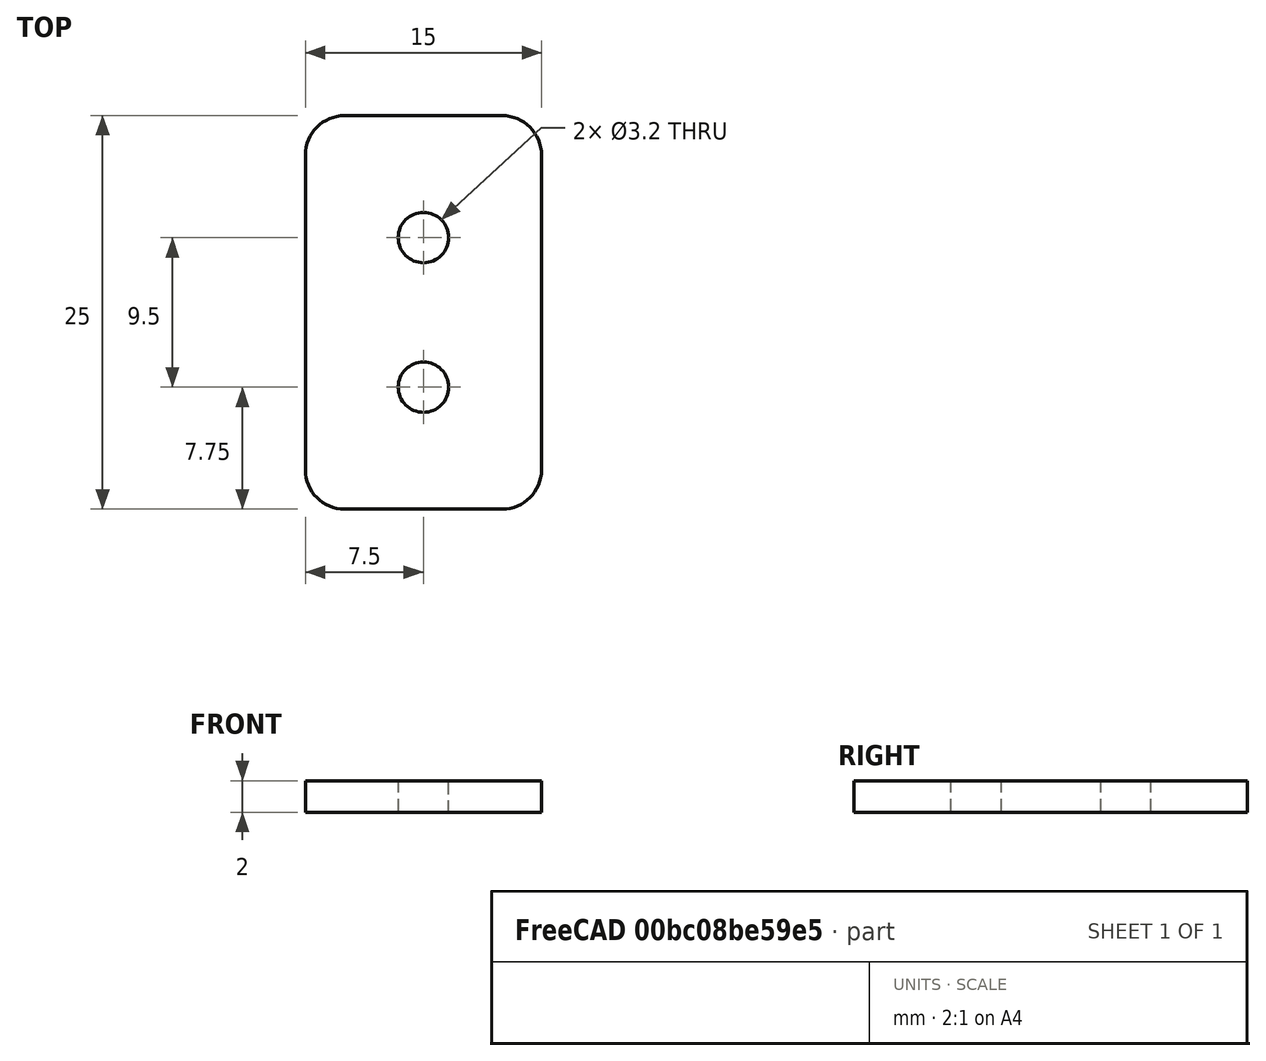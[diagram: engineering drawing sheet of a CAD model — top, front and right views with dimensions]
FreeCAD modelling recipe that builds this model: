
FCSTD DOCUMENT  (FreeCAD 1.0R39109 (Git))
Label: joint_plates_m3
License: All rights reserved
LicenseURL: https://en.wikipedia.org/wiki/All_rights_reserved
objects: Sketcher::SketchObject×1, PartDesign::Pad×1, PartDesign::Body×1
note: 6 computed .brp shape members not serialized (recipe doc carries the construction recipe); baked Part::Feature solids carry a one-line shape summary decoded from their .brp

FEATURE [Sketcher::SketchObject] Sketch
  ArcFitTolerance = 1e-06
  AttachmentSupport = -> [XY_Plane]
  FullyConstrained = true
  MakeInternals = false
  MapMode = 5
  sketch-geometry (12):
    g0: Circle CenterX=0 CenterY=4.75 CenterZ=0 NormalX=0 NormalY=0 NormalZ=1 AngleXU=0 Radius=1.6
    g1: Circle CenterX=0 CenterY=-4.75 CenterZ=0 NormalX=0 NormalY=0 NormalZ=1 AngleXU=0 Radius=1.6
    g2: LineSegment StartX=-7.5 StartY=10 StartZ=0 EndX=-7.5 EndY=-10 EndZ=0
    g3: LineSegment StartX=-5 StartY=-12.5 StartZ=0 EndX=5 EndY=-12.5 EndZ=0
    g4: LineSegment StartX=7.5 StartY=-10 StartZ=0 EndX=7.5 EndY=10 EndZ=0
    g5: LineSegment StartX=5 StartY=12.5 StartZ=0 EndX=-5 EndY=12.5 EndZ=0
    g6: ArcOfCircle CenterX=-5 CenterY=10 CenterZ=0 NormalX=0 NormalY=0 NormalZ=1 AngleXU=0 Radius=2.5 StartAngle=1.5708 EndAngle=3.14159
    g7: ArcOfCircle CenterX=-5 CenterY=-10 CenterZ=0 NormalX=0 NormalY=0 NormalZ=1 AngleXU=0 Radius=2.5 StartAngle=3.14159 EndAngle=4.71239
    g8: ArcOfCircle CenterX=5 CenterY=-10 CenterZ=0 NormalX=0 NormalY=0 NormalZ=1 AngleXU=0 Radius=2.5 StartAngle=4.71239 EndAngle=6.28319
    g9: ArcOfCircle CenterX=5 CenterY=10 CenterZ=0 NormalX=0 NormalY=0 NormalZ=1 AngleXU=0 Radius=2.5 StartAngle=3e-16 EndAngle=1.5708
    g10: GeomPoint [constr] X=-7.5 Y=12.5 Z=0
    g11: GeomPoint [constr] X=7.5 Y=-12.5 Z=0
  constraints (28):
    c: PointOnObject(g0,g-2)
    c: Tangent(g2,g6) = -1.5708
    c: Tangent(g2,g7) = -1.5708
    c: Tangent(g3,g7) = -1.5708
    c: Tangent(g3,g8) = -1.5708
    c: Tangent(g4,g8) = -1.5708
    c: Tangent(g4,g9) = -1.5708
    c: Tangent(g5,g9) = -1.5708
    c: Tangent(g5,g6) = -1.5708
    c: Vertical(g2)
    c: Vertical(g4)
    c: Horizontal(g3)
    c: Horizontal(g5)
    c: Equal(g6,g7)
    c: Equal(g7,g8)
    c: Equal(g8,g9)
    c: PointOnObject(g10,g2)
    c: PointOnObject(g10,g5)
    c: PointOnObject(g11,g3)
    c: PointOnObject(g11,g4)
    c: DistanceX(g2,g4) = 15
    c: Equal(g1,g0)
    c: Symmetric(g1,g0,g-1)
    c: Radius(g0) = 1.6
    c: Symmetric(g11,g10,g-1)
    c: DistanceY(g1,g0) = 9.5
    c: DistanceY(g3,g5) = 25
    c: Radius(g8) = 2.5
FEATURE [PartDesign::Pad] Pad  label="JointPad"
  Direction = (0,0,1)
  Length = 2
  Length2 = 10
  Profile = -> Sketch
  ReferenceAxis = -> Sketch [N_Axis]
  Refine = true
  Suppressed = false
  Type = 0
FEATURE [PartDesign::Body] Body  label="joint_plates_m3"
  AllowCompound = false
  Group = -> [Sketch,Pad]
  Origin = -> Origin
  Tip = -> Pad
